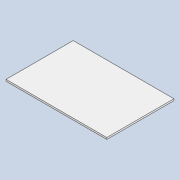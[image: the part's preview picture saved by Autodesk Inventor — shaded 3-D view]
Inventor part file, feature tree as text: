
AUTODESK INVENTOR PART (.ipt)
format: ipt  version: 2022 (Build 260153000, 153)  size: 84,992 bytes
history: native  units: in
note: dims shown in document units (in); Inventor stores cm internally (conversion verified against a paired STEP export)
features: other x1, extrude x1, sketch x1
ambient origin geometry x8: Origin, YZ Plane, XZ Plane, XY Plane, X Axis, Y Axis, Z Axis, Center Point
bodies: Body1 (feature_tree)
feature tree (3):
  other  "ソリッド1"
  extrude  "押し出し1"  Depth=11.811in
  sketch  "スケッチ1"
